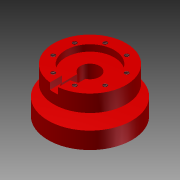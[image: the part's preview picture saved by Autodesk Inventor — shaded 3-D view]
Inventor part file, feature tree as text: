
AUTODESK INVENTOR PART (.ipt)
format: ipt  version: 2012 SP1 (Build 160190100, 190)  size: 248,832 bytes
history: native  units: in
note: dims shown in document units (in); Inventor stores cm internally (conversion verified against a paired STEP export)
features: sketch x5, extrude x3, revolve x1, hole x1, pattern_circular x1
ambient origin geometry x8: Origin, YZ Plane, XZ Plane, XY Plane, X Axis, Y Axis, Z Axis, Center Point
bodies: Solid1 (feature_tree)
feature tree (11):
  revolve  "Revolution1"  [1 undecoded]
  hole  "Hole3"  [1 undecoded]
  pattern_circular  "Circular Pattern2"  [2 undecoded]
  extrude  "Extrusion1"  Depth=0.1935in
  extrude  "Extrusion2"  Depth=0.2345in
  extrude  "Extrusion4"  Depth=0.1575in
  sketch  "Sketch1"  dims[d1=0.886in d2=1.025in]
  sketch  "Sketch4"  dims[d3=0.4925in d7=0.412in]
  sketch  "Sketch5"  dims[d8=90.0deg]
  sketch  "Sketch7"  dims[d32=0.412in]
  sketch  "Sketch12"  dims[d33=1.1in d36=0.8268in d37=0.1935in d38=0.2345in d39=0.1575in d40=0.06in d42=0.488in d43=0.35in d45=0.104in d46=0.4154in d47=0.1575in d48=0.0787in d49=90.0deg d50=0.315in d51=0.0in d52=3.1496in d53=360.0deg d57=0.0in d58=0.156in d59=0.0in d60=0.526in d61=0.0in d86=0.9765in d87=0.087in d88=0.8705in d89=0.414in d90=0.309in d91=0.087in d93=0.125in d94=0.5906in d95=0.0in d99=1.0763in d100=0.689in d102=22.5deg d103=0.4925in d104=0.5267in d105=0.9455in d106=1.19in d107=0.1in]
note: 4 required parameter values undecoded (feature->parameter linkage not recoverable at this tier; creation-order binding heuristic only, values carry confidence <= 0.55)